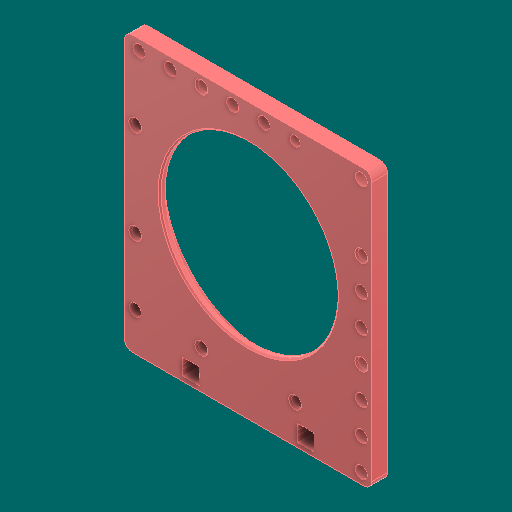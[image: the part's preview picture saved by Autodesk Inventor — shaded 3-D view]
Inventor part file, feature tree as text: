
AUTODESK INVENTOR PART (.ipt)
format: ipt  version: 2023.1 (Build 271208000, 208)  size: 246,784 bytes
history: native  units: in
note: dims shown in document units (in); Inventor stores cm internally (conversion verified against a paired STEP export)
features: other x3, sketch x2
ambient origin geometry x8: Origin, YZ Plane, XZ Plane, XY Plane, X Axis, Y Axis, Z Axis, Center Point
bodies: Solid1 (feature_tree)
feature tree (5):
  other  "Baseplate.ipt"
  other  "Solid1::Baseplate.ipt"
  other  "TaggingFeature1"
  sketch  "Sketch1"  dims[d0=0.3937in]
  sketch  "Sketch2"
